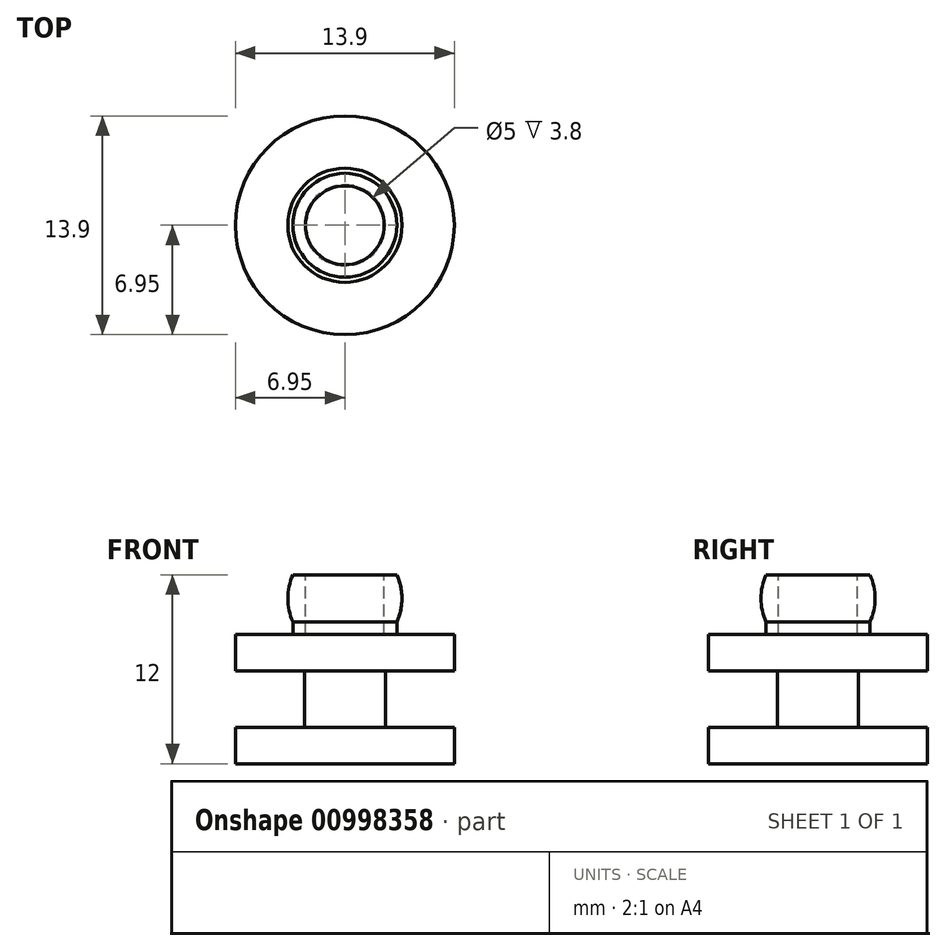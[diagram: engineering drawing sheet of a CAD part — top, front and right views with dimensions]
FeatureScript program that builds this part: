
annotation { "Feature Type Name" : "Feature", "Feature Type Description" : "" }
export const myFeature = defineFeature(function(context is Context, id is Id, definition is map)
    precondition{}
    {
        {
            var Q0;
            Q0=qCreatedBy(makeId("Top.planeOp"),FACE);
            var sketch = newSketch(context, id + "F0", { "sketchPlane" : qUnion([Q0])});
            skCircle(sketch, "E0", {"center": v(0, 0) * mm, "radius": 6.95 * mm});
            skSolve(sketch);
        }
        {
            var Q0;
            Q0 = qSketchRegion(id + "F0", true);
            extrude(context, id + "F1", {"entities" : qUnion([Q0]), "depth" : 2.3 * mm, "offsetDistance" : 25 * mm});
        }
        {
            var Q0;
            Q0=makeQuery(id+"F1.opExtrude","CAP_FACE",FACE,{"disambiguationData":[OSD([sQuery(id+"F0.wireOp",EDGE,"E0")])],"isStart":false});
            var sketch = newSketch(context, id + "F2", { "sketchPlane" : qUnion([Q0])});
            skCircle(sketch, "E1", {"center": v(0, 0) * mm, "radius": 2.58 * mm});
            skSolve(sketch);
        }
        {
            var Q0;
            Q0 = qSketchRegion(id + "F2", true);
            extrude(context, id + "F3", {"entities" : qUnion([Q0]), "operationType" : NewBodyOperationType.ADD, "depth" : 3.6 * mm, "offsetDistance" : 25 * mm});
        }
        {
            var Q0;
            Q0=makeQuery(id+"F3.opExtrude","CAP_FACE",FACE,{"disambiguationData":[OSD([sQuery(id+"F2.wireOp",EDGE,"E1")])],"isStart":false});
            var sketch = newSketch(context, id + "F4", { "sketchPlane" : qUnion([Q0])});
            skCircle(sketch, "E2.0", {"center": v(0, 0) * mm, "radius": 6.95 * mm});
            skSolve(sketch);
        }
        {
            var Q0;
            Q0 = qSketchRegion(id + "F4", true);
            extrude(context, id + "F5", {"entities" : qUnion([Q0]), "operationType" : NewBodyOperationType.ADD, "depth" : 2.3 * mm, "offsetDistance" : 25 * mm});
        }
        {
            var Q0;
            Q0=makeQuery(id+"F5.opExtrude","CAP_FACE",FACE,{"disambiguationData":[OSD([sQuery(id+"F4.wireOp",EDGE,"E2.0")])],"isStart":false});
            var sketch = newSketch(context, id + "F6", { "sketchPlane" : qUnion([Q0])});
            skCircle(sketch, "E3", {"center": v(0, 0) * mm, "radius": 3.3 * mm});
            skSolve(sketch);
        }
        {
            var Q0;
            Q0=makeQuery(id+"F6.imprint","IMPRINT",FACE,{"disambiguationData":[TD([[makeQuery(id+"F6.imprint","IMPRINT",EDGE,{"derivedFrom":sQuery(id+"F6.wireOp",EDGE,"E3")}),1.0]])]});
            var Q1;
            Q1=sQuery(id+"F6.wireOp",EDGE,"E3");
            extrude(context, id + "F7", {"entities" : qUnion([Q0]), "operationType" : NewBodyOperationType.ADD, "surfaceEntities" : qUnion([Q1]), "depth" : 3.8 * mm, "offsetDistance" : 25 * mm});
        }
        {
            var Q0;
            Q0=qCreatedBy(makeId("Front.planeOp"),FACE);
            var sketch = newSketch(context, id + "F8", { "sketchPlane" : qUnion([Q0])});
            skLineSegment(sketch, "E4", {"start": v(-3.3, 9) * mm, "end": v(-3.3, 12) * mm});
            skArc(sketch, "E5", {"start": v(-3.3, 12) * mm, "mid": v(-3.62, 10.5) * mm, "end": v(-3.3, 9) * mm});
            skLineSegment(sketch, "E6", {"start": v(0, 0) * mm, "end": v(0, 13.68) * mm, "construction": true});
            skPoint(sketch, "E7.orphan", {"position": v(-3.3, 8.2) * mm});
            skSolve(sketch);
        }
        {
            var Q0;
            Q0 = qSketchRegion(id + "F8", true);
            var Q1;
            Q1=makeQuery(id+"F7.opExtrude","SWEPT_FACE",FACE,{"disambiguationData":[OSD([sQuery(id+"F6.wireOp",EDGE,"E3")])]});
            revolve(context, id + "F9", {"operationType" : NewBodyOperationType.ADD, "surfaceOperationType" : NewSurfaceOperationType.NEW, "entities" : qUnion([Q0]), "axis" : qUnion([Q1]), "revolveType" : RevolveType.FULL});
        }
        {
            var Q0;
            Q0=makeQuery(id+"F7.opExtrude","CAP_FACE",FACE,{"disambiguationData":[OSD([sQuery(id+"F6.wireOp",EDGE,"E3")])],"isStart":false});
            var sketch = newSketch(context, id + "F10", { "sketchPlane" : qUnion([Q0])});
            skCircle(sketch, "E8", {"center": v(0, 0) * mm, "radius": 2.5 * mm});
            skSolve(sketch);
        }
        {
            var Q0;
            Q0 = qSketchRegion(id + "F10", true);
            var Q1;
            Q1=makeQuery(id+"F5.opExtrude","CAP_FACE",FACE,{"disambiguationData":[OSD([sQuery(id+"F4.wireOp",EDGE,"E2.0")])],"isStart":false});
            extrude(context, id + "F11", {"entities" : qUnion([Q0]), "operationType" : NewBodyOperationType.REMOVE, "endBound" : BoundingType.UP_TO_SURFACE, "oppositeDirection" : true, "depth" : 25 * mm, "endBoundEntityFace" : qUnion([Q1]), "offsetDistance" : 25 * mm});
        }
    });
